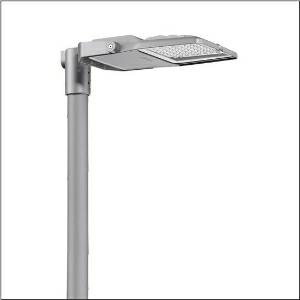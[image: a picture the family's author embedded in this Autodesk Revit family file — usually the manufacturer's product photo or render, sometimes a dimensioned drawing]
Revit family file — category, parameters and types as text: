
# Revit family: floodlight_fl_21_iq_mini___pl43_5xa7772d4a3a_0702
name_source: partatom
category: Lighting Fixtures
units: mm (PartAtom-declared; Revit-internal decimal feet)

## family parameters
Cut with Voids When Loaded = No
Host = Face
Light Source = No
Part Type = Normal
Room Calculation Point = No
Round Connector Dimension = Use Diameter
Shared = No

## types (1)
- --- (1 x LED, 19090 lm, 143 W, 4000K)
    Apparent Load = 143 VA
    CIE Flux Codes = 27 78 99 100 100
    Color Rendering = 70
    Color Temperature = 4000K
    Default Elevation = 1800 mm
    Description = Floodlight FL 21 iQ mini, floodlight, primary light control with lens, of PMMA, primary optical cover: protective disc, of toughened safety glass, transparent, light distribution: PL43, light emission: direct distribution, installation type: surface-mounted, LED, High Power LED, rated luminous flux: 19.090lm, luminous efficacy: 134lm/W, light colour: 740, colour temperature: 4000K, control gear: iQ Street-Remote/DALI, control: Auto-Match, Temp-Guard, Night-Set, Smart-Wire, Desk-Remote (wireless, voltage-free reading and setting of iQ features in the workshop via application-optimized NFC function/RFID function), optimised constant luminous flux control (CLO 2.0), Light-Fading, Lumen-Switch, with terminal, 6-pole, mains connection: 220..240V, AC, 50/60Hz, start of lifetime: 143W, end of service life: 152W, reduction: 61W, luminaire housing, of diecast aluminium, powder-coated, Siteco® metallic grey (DB 702S), corrosivity category C5 mid according to DIN EN ISO 12944, suitable for swimming pools, chlorine-resistant, sealing non-destructively replaceable, please order mast flange separately, mast bracket, of steel, galvanised, powder-coated, protection rating (complete): IP66, insulation class (complete): insulation class II (safety insulation), certification: CE, ENEC, VDE, protection symbol: D, impact resistance: IK08, permissible operating ambient temperature: -40..+40°C, permissible operating ambient temperature for outdoor applications: -40..+50°C, standard: DIN EN 12944, LABS conformity tested according to VDMA 24364:2018-05, packaging unit: 1 piece

Light Distribution: PL43
    Height = 70 mm
    Lamp = 1 x LED
    Lamp Light Flux = 19090 lm
    Lamp Power = 143 W
    Lamp count = 1
    Length = 485 mm
    Luminous efficacy = 133 lm/W
    Manufacturer = Siteco
    ModVariant = No
    Model = 5XA7772D4A3A
    Number of Poles = 1
    OnlyDefault = Yes
    Power Factor = 1
    Product Name = Floodlight FL 21 iQ mini | PL43
    Product group = floodlight | pylon annexe
    ProductGroupID = 6201
    Protection Class = Protection class II
    Protection Degree = IP 66
    RLX_Detail_Level = 1
    RLX_Emergency_Light_Flux = 0 lm
    RLX_Emergency_Type = 0
    RLX_Emergency_Type_DB = No
    RlxData = <blob elided: 101545 chars, md5=d94e21d0>
    Socket = socket
    Standby Power = 0 W
    System Light Flux = 19090 lm
    System Power = 143 W
    Type Comments = factory setting: luminous flux: 100 % | dim-lin: 254 | 730 mA
    Type Image = l_1007125.jpg
    URL = http://relux.com
    VarID = @adj_182923
    Voltage = 0 V
    Weight = 0.00 kg
    Width = 337 mm

## geometry (parser evidence)
native form markers: Blend x4, Sweep x12
no freeform markers — native parametric forms only
